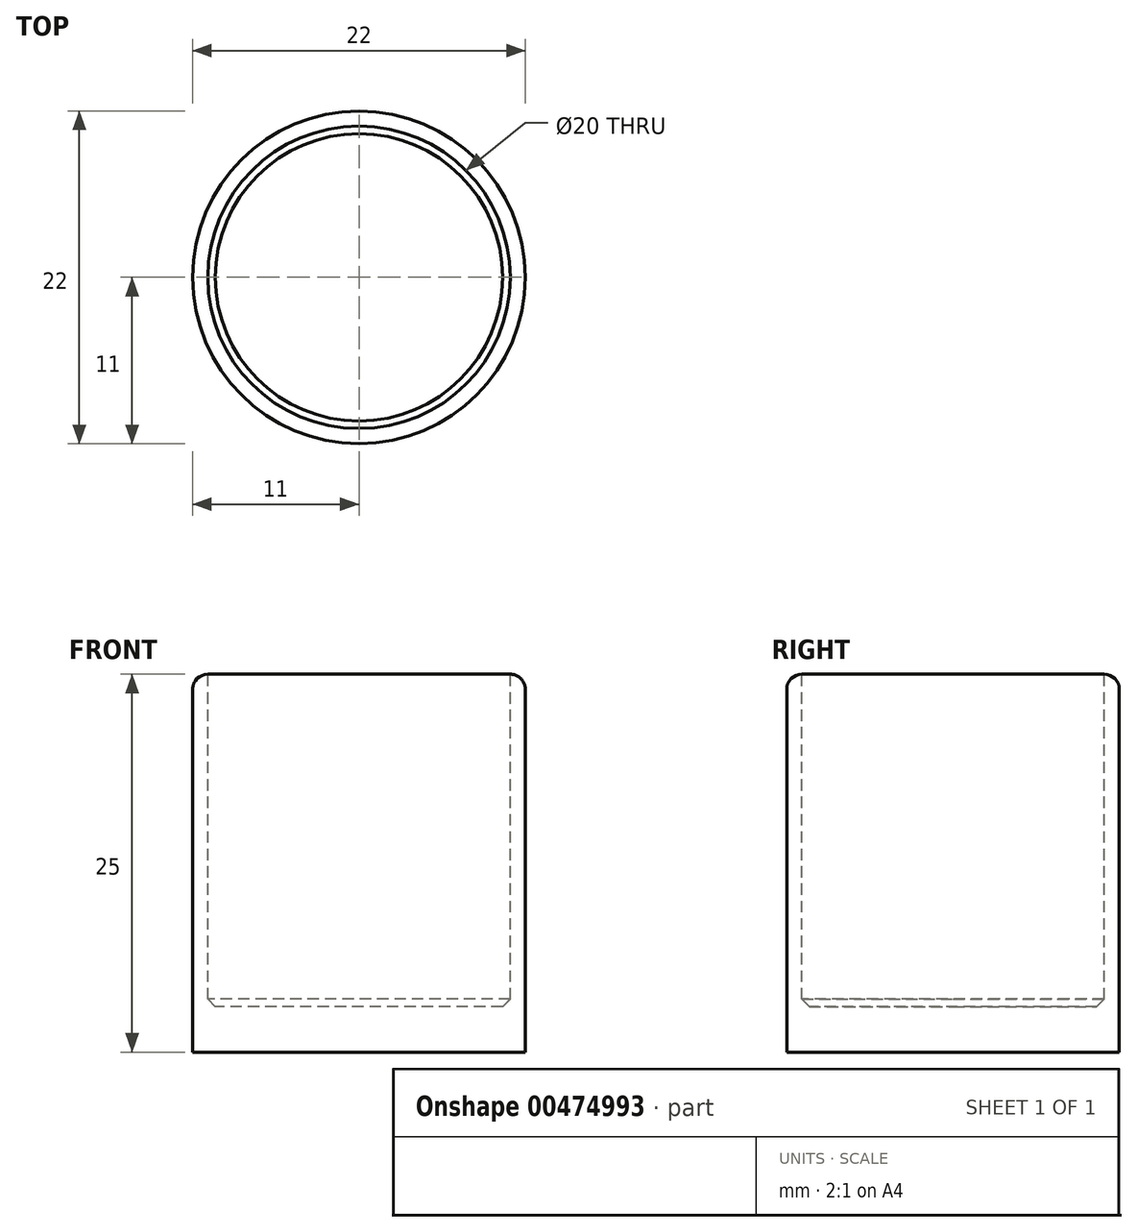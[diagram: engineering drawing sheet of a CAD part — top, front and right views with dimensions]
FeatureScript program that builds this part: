
annotation { "Feature Type Name" : "Feature", "Feature Type Description" : "" }
export const myFeature = defineFeature(function(context is Context, id is Id, definition is map)
    precondition{}
    {
        {
            var Q0;
            Q0=qCreatedBy(makeId("Top.planeOp"),FACE);
            var sketch = newSketch(context, id + "F0", { "sketchPlane" : qUnion([Q0])});
            skCircle(sketch, "E0", {"center": v(0, 0) * mm, "radius": 11 * mm});
            skSolve(sketch);
        }
        {
            var Q0;
            Q0 = qSketchRegion(id + "F0", true);
            extrude(context, id + "F1", {"entities" : qUnion([Q0]), "depth" : 25 * mm});
        }
        {
            var Q0;
            Q0=makeQuery(id+"F1.opExtrude","CAP_FACE",FACE,{"disambiguationData":[OSD([sQuery(id+"F0.wireOp",EDGE,"E0")])],"isStart":false});
            var sketch = newSketch(context, id + "F2", { "sketchPlane" : qUnion([Q0])});
            skCircle(sketch, "E1", {"center": v(0, 0) * mm, "radius": 10 * mm});
            skSolve(sketch);
        }
        {
            var Q0;
            Q0 = qSketchRegion(id + "F2", true);
            extrude(context, id + "F3", {"entities" : qUnion([Q0]), "operationType" : NewBodyOperationType.REMOVE, "oppositeDirection" : true, "depth" : 22 * mm});
        }
        {
            var Q0;
            Q0=makeQuery(id+"F3.boolean.opBoolean","COPY",EDGE,{"derivedFrom":makeQuery(id+"F3.opExtrude","CAP_EDGE",EDGE,{"disambiguationData":[OSD([sQuery(id+"F2.wireOp",EDGE,"E1")])],"isStart":false})});
            chamfer(context, id + "F4", {"entities" : qUnion([Q0]), "width" : 0.5 * mm, "tangentPropagation" : true});
        }
        {
            var Q0;
            Q0=makeQuery(id+"F1.opExtrude","CAP_EDGE",EDGE,{"disambiguationData":[OSD([sQuery(id+"F0.wireOp",EDGE,"E0")])],"isStart":false});
            fillet(context, id + "F5", {"entities" : qUnion([Q0]), "radius" : 1 * mm, "tangentPropagation" : true, "allowEdgeOverflow" : false});
        }
    });
